# Revit family: 71_98_0551_B
name_source: partatom
category: Communication Devices
revit_build: Autodesk Revit 2015 (Build: 20141119_1515(x64)
units: mm (PartAtom-declared; Revit-internal decimal feet)

## types (1)
- 71_98_0551_B
    Basisplaat = Basisplaat
    Breedte = 50 mm  [stored 0.164042 ft]
    Consumption = 2 W
    Default Elevation = 1219 mm
    Diepte = 90 mm
    Jack = Jack
    Kabel = Kabel
    Knoppen = Basisplaat
    Lengte = 155 mm  [stored 0.50853 ft]
    Manufacturer = Televic Conference
    Model = Confidea F-CS
    Onderplaat = Inox
    Product ID = 71.98.0551
    Scherm = Jack
    Schroef = Basisplaat
    Type Comments = Confidea Flushmount Channel Selector
    URL = http://www.televic-conference.com
    Voltage = 48 V
    Weight = 220

note: [stored X ft] marks values corroborated as IEEE doubles in the binary element streams (Revit-internal decimal feet)

## geometry (parser evidence)
native form markers: Sweep x2
no freeform markers — native parametric forms only
